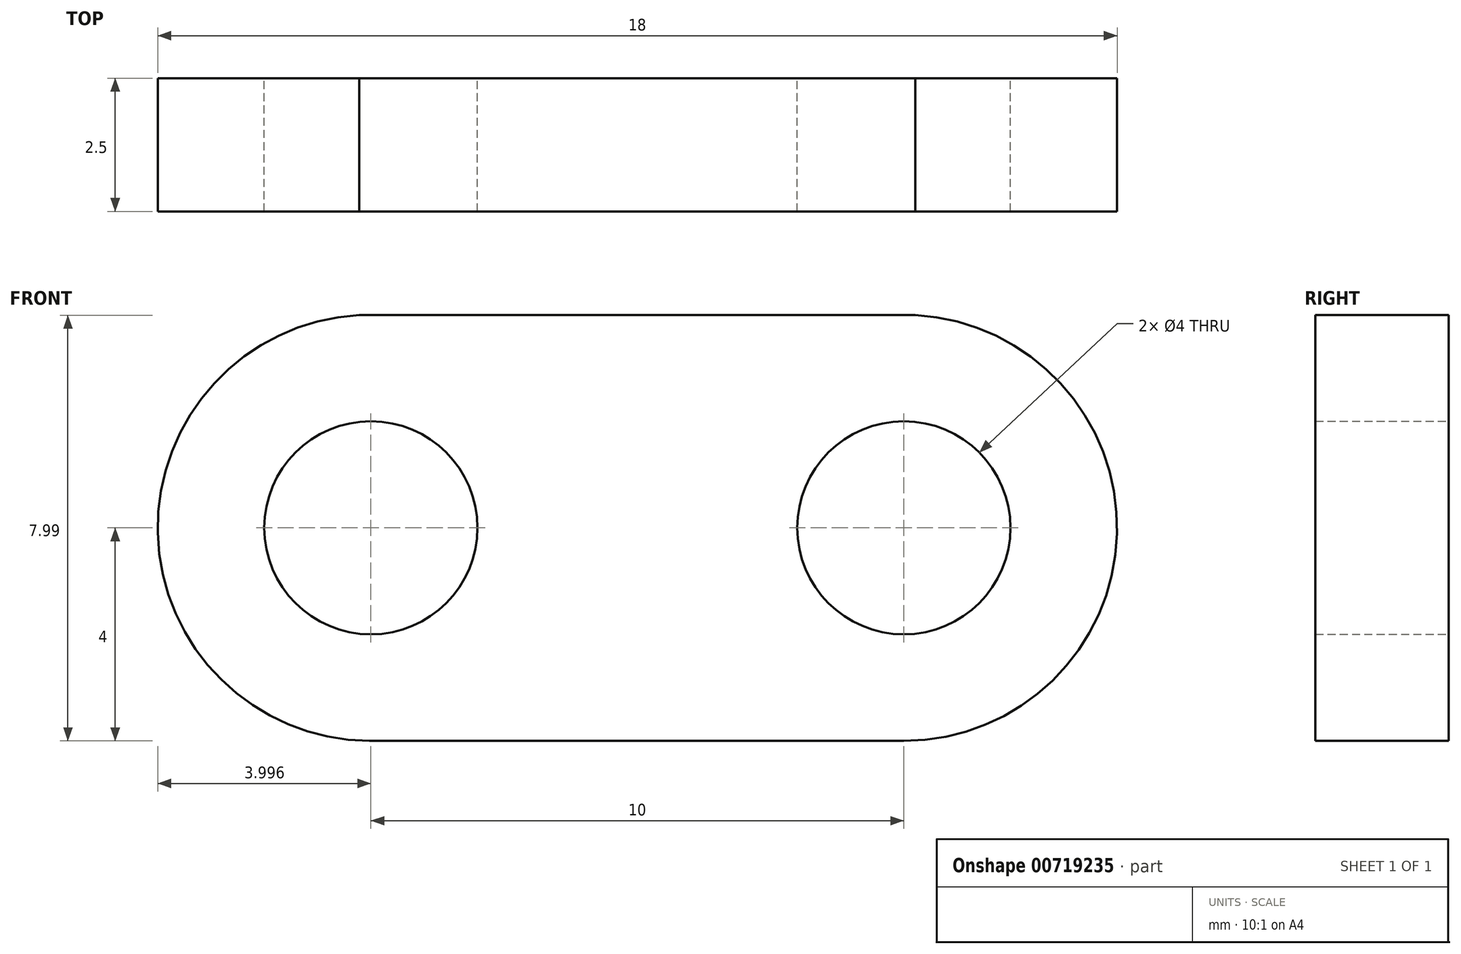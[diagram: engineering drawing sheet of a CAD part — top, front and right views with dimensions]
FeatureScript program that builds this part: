
annotation { "Feature Type Name" : "Feature", "Feature Type Description" : "" }
export const myFeature = defineFeature(function(context is Context, id is Id, definition is map)
    precondition{}
    {
        {
            var Q0;
            Q0=qCreatedBy(makeId("Front.planeOp"),FACE);
            var sketch = newSketch(context, id + "F0", { "sketchPlane" : qUnion([Q0])});
            skLineSegment(sketch, "E0", {"start": v(-4.38, 0) * mm, "end": v(5.62, 0) * mm});
            skCircle(sketch, "E1", {"center": v(-4.38, 0) * mm, "radius": 2 * mm});
            skArc(sketch, "E2", {"start": v(-4.17, 4) * mm, "mid": v(-8.38, 0.1) * mm, "end": v(-4.36, -4) * mm});
            skCircle(sketch, "E3", {"center": v(5.62, 0) * mm, "radius": 2 * mm});
            skArc(sketch, "E4", {"start": v(5.62, -4) * mm, "mid": v(9.61, 0.1) * mm, "end": v(5.4, 4) * mm});
            skLineSegment(sketch, "E5", {"start": v(-4.6, 4) * mm, "end": v(5.83, 4) * mm});
            skLineSegment(sketch, "E6", {"start": v(-4.41, -4) * mm, "end": v(5.62, -4) * mm});
            skSolve(sketch);
        }
        {
            var Q0;
            Q0=makeQuery(id+"F0.imprint","IMPRINT",FACE,{"disambiguationData":[TD([[makeQuery(id+"F0.imprint","IMPRINT",EDGE,{"derivedFrom":sQuery(id+"F0.wireOp",EDGE,"E1")}),-1.0]])]});
            extrude(context, id + "F1", {"entities" : qUnion([Q0]), "depth" : 2.5 * mm, "offsetDistance" : 25.4 * mm});
        }
    });
